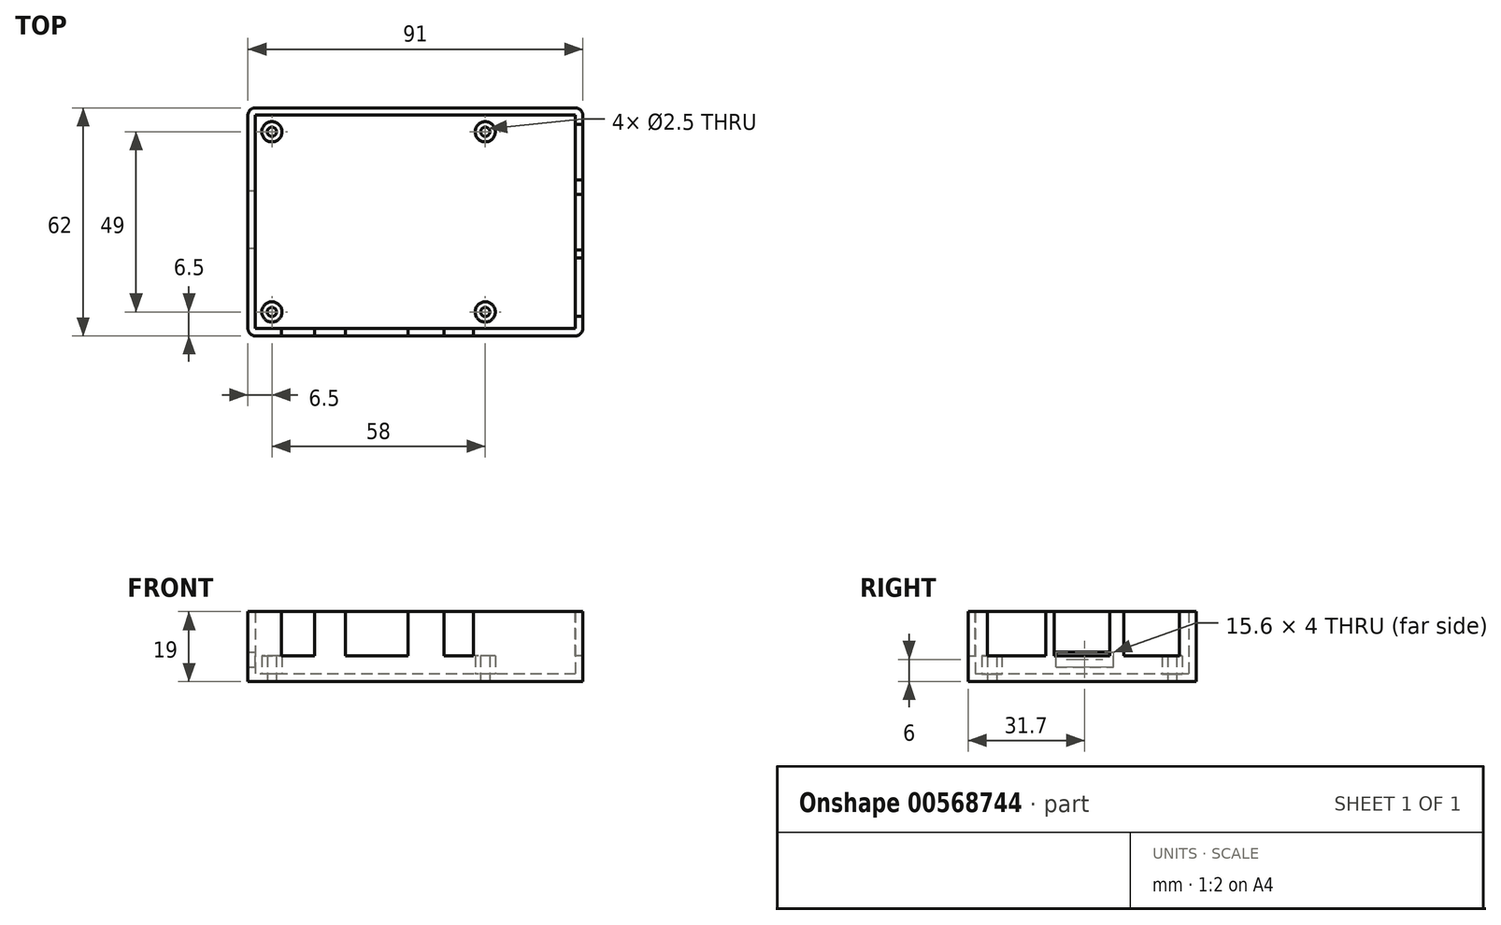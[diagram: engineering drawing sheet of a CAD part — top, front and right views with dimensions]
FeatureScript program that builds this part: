
annotation { "Feature Type Name" : "Feature", "Feature Type Description" : "" }
export const myFeature = defineFeature(function(context is Context, id is Id, definition is map)
    precondition{}
    {
        {
            var Q0;
            Q0=qCreatedBy(makeId("Top.planeOp"),FACE);
            var sketch = newSketch(context, id + "F0", { "sketchPlane" : qUnion([Q0])});
            skLineSegment(sketch, "E0.bottom", {"start": v(0, 0) * mm, "end": v(91, 0) * mm});
            skLineSegment(sketch, "E0.top", {"start": v(0, 62) * mm, "end": v(91, 62) * mm});
            skLineSegment(sketch, "E0.left", {"start": v(0, 0) * mm, "end": v(0, 62) * mm});
            skLineSegment(sketch, "E0.right", {"start": v(91, 0) * mm, "end": v(91, 62) * mm});
            skLineSegment(sketch, "E1.0", {"start": v(2, 60) * mm, "end": v(89, 60) * mm});
            skLineSegment(sketch, "E1.1", {"start": v(2, 2) * mm, "end": v(2, 60) * mm});
            skLineSegment(sketch, "E1.2", {"start": v(2, 2) * mm, "end": v(89, 2) * mm});
            skLineSegment(sketch, "E1.3", {"start": v(89, 2) * mm, "end": v(89, 60) * mm});
            skLineSegment(sketch, "E2.0", {"start": v(3, 59) * mm, "end": v(88, 59) * mm, "construction": true});
            skLineSegment(sketch, "E2.1", {"start": v(3, 3) * mm, "end": v(3, 59) * mm, "construction": true});
            skLineSegment(sketch, "E2.2", {"start": v(3, 3) * mm, "end": v(88, 3) * mm, "construction": true});
            skLineSegment(sketch, "E2.3", {"start": v(88, 3) * mm, "end": v(88, 59) * mm, "construction": true});
            skSolve(sketch);
        }
        {
            var Q0;
            Q0=makeQuery(id+"F0.imprint","IMPRINT",FACE,{"disambiguationData":[TD([[makeQuery(id+"F0.imprint","IMPRINT",EDGE,{"derivedFrom":sQuery(id+"F0.wireOp",EDGE,"E0.bottom")}),1.0]])]});
            var Q1;
            Q1=makeQuery(id+"F0.imprint","IMPRINT",FACE,{"disambiguationData":[TD([[makeQuery(id+"F0.imprint","IMPRINT",EDGE,{"derivedFrom":sQuery(id+"F0.wireOp",EDGE,"E1.0")}),-1.0]])]});
            var Q2;
            Q2=makeQuery(id+"F0.imprint","IMPRINT",FACE,{"disambiguationData":[TD([[makeQuery(id+"F0.imprint","IMPRINT",EDGE,{"derivedFrom":sQuery(id+"F0.wireOp",EDGE,"70Z1q3uj-Ijsq-j34Q-QLTl-TNYluKwycWAc")}),-1.0]])]});
            var Q3;
            Q3=makeQuery(id+"F0.imprint","IMPRINT",FACE,{"disambiguationData":[TD([[makeQuery(id+"F0.imprint","IMPRINT",EDGE,{"derivedFrom":sQuery(id+"F0.wireOp",EDGE,"70Z1q3uj-Ijsq-j34Q-QLTl-TNYluKwycWAc")}),1.0]])]});
            var Q4;
            Q4=makeQuery(id+"F0.imprint","IMPRINT",FACE,{"disambiguationData":[TD([[makeQuery(id+"F0.imprint","IMPRINT",EDGE,{"derivedFrom":sQuery(id+"F0.wireOp",EDGE,"oQS00QZW-vNgy-keFn-j1EO-3NQ6BuG1DB5t")}),1.0]])]});
            var Q5;
            Q5=makeQuery(id+"F0.imprint","IMPRINT",FACE,{"disambiguationData":[TD([[makeQuery(id+"F0.imprint","IMPRINT",EDGE,{"derivedFrom":sQuery(id+"F0.wireOp",EDGE,"oQS00QZW-vNgy-keFn-j1EO-3NQ6BuG1DB5t")}),-1.0]])]});
            var Q6;
            Q6=makeQuery(id+"F0.imprint","IMPRINT",FACE,{"disambiguationData":[TD([[makeQuery(id+"F0.imprint","IMPRINT",EDGE,{"derivedFrom":sQuery(id+"F0.wireOp",EDGE,"wAKH25U2-zgrz-eWns-j4sG-55EGYDsWBGuE")}),-1.0]])]});
            var Q7;
            Q7=makeQuery(id+"F0.imprint","IMPRINT",FACE,{"disambiguationData":[TD([[makeQuery(id+"F0.imprint","IMPRINT",EDGE,{"derivedFrom":sQuery(id+"F0.wireOp",EDGE,"wAKH25U2-zgrz-eWns-j4sG-55EGYDsWBGuE")}),1.0]])]});
            var Q8;
            Q8=makeQuery(id+"F0.imprint","IMPRINT",FACE,{"disambiguationData":[TD([[makeQuery(id+"F0.imprint","IMPRINT",EDGE,{"derivedFrom":sQuery(id+"F0.wireOp",EDGE,"CY4kjaGw-B2gw-ZOHd-aq1m-nUtJw6pQ65pw")}),-1.0]])]});
            var Q9;
            Q9=makeQuery(id+"F0.imprint","IMPRINT",FACE,{"disambiguationData":[TD([[makeQuery(id+"F0.imprint","IMPRINT",EDGE,{"derivedFrom":sQuery(id+"F0.wireOp",EDGE,"CY4kjaGw-B2gw-ZOHd-aq1m-nUtJw6pQ65pw")}),1.0]])]});
            extrude(context, id + "F1", {"entities" : qUnion([Q0, Q1, Q2, Q3, Q4, Q5, Q6, Q7, Q8, Q9]), "depth" : 2 * mm, "offsetDistance" : 25 * mm});
        }
        {
            var Q0;
            Q0 = qSketchRegion(id + "F0", true);
            extrude(context, id + "F2", {"entities" : qUnion([Q0]), "operationType" : NewBodyOperationType.ADD, "depth" : 19 * mm, "offsetDistance" : 25 * mm});
        }
        {
            var Q0;
            Q0=makeQuery(id+"F1.opExtrude","CAP_FACE",FACE,{"disambiguationData":[OSD([sQuery(id+"F0.wireOp",EDGE,"E0.bottom"),sQuery(id+"F0.wireOp",EDGE,"E0.top"),sQuery(id+"F0.wireOp",EDGE,"E0.left"),sQuery(id+"F0.wireOp",EDGE,"E0.right")])],"isStart":false});
            var sketch = newSketch(context, id + "F3", { "sketchPlane" : qUnion([Q0])});
            skCircle(sketch, "E3", {"center": v(6.5, 55.5) * mm, "radius": 1.25 * mm});
            skCircle(sketch, "E4", {"center": v(6.5, 55.5) * mm, "radius": 2.75 * mm});
            skCircle(sketch, "E5", {"center": v(64.5, 55.5) * mm, "radius": 1.25 * mm});
            skCircle(sketch, "E6", {"center": v(64.5, 55.5) * mm, "radius": 2.75 * mm});
            skCircle(sketch, "E7", {"center": v(64.5, 6.5) * mm, "radius": 1.25 * mm});
            skCircle(sketch, "E8", {"center": v(64.5, 6.5) * mm, "radius": 2.75 * mm});
            skCircle(sketch, "E9", {"center": v(6.5, 6.5) * mm, "radius": 1.25 * mm});
            skCircle(sketch, "E10", {"center": v(6.5, 6.5) * mm, "radius": 2.75 * mm});
            skSolve(sketch);
        }
        {
            var Q0;
            Q0 = qSketchRegion(id + "F3", true);
            extrude(context, id + "F4", {"entities" : qUnion([Q0]), "operationType" : NewBodyOperationType.ADD, "depth" : 5 * mm, "offsetDistance" : 25 * mm});
        }
        {
            var Q0;
            Q0=makeQuery(id+"F4.boolean.opBoolean","SPLIT",FACE,{"disambiguationData":[TD([makeQuery(id+"F4.opExtrude","SWEPT_FACE",FACE,{"disambiguationData":[OSD([sQuery(id+"F3.wireOp",EDGE,"E3")])]})])],"derivedFrom":makeQuery(id+"F1.opExtrude","CAP_FACE",FACE,{"disambiguationData":[OSD([sQuery(id+"F0.wireOp",EDGE,"E0.bottom"),sQuery(id+"F0.wireOp",EDGE,"E0.top"),sQuery(id+"F0.wireOp",EDGE,"E0.left"),sQuery(id+"F0.wireOp",EDGE,"E0.right")])],"isStart":false})});
            var Q1;
            Q1=makeQuery(id+"F4.boolean.opBoolean","SPLIT",FACE,{"disambiguationData":[TD([makeQuery(id+"F4.opExtrude","SWEPT_FACE",FACE,{"disambiguationData":[OSD([sQuery(id+"F3.wireOp",EDGE,"E5")])]})])],"derivedFrom":makeQuery(id+"F1.opExtrude","CAP_FACE",FACE,{"disambiguationData":[OSD([sQuery(id+"F0.wireOp",EDGE,"E0.bottom"),sQuery(id+"F0.wireOp",EDGE,"E0.top"),sQuery(id+"F0.wireOp",EDGE,"E0.left"),sQuery(id+"F0.wireOp",EDGE,"E0.right")])],"isStart":false})});
            var Q2;
            Q2=makeQuery(id+"F4.boolean.opBoolean","SPLIT",FACE,{"disambiguationData":[TD([makeQuery(id+"F4.opExtrude","SWEPT_FACE",FACE,{"disambiguationData":[OSD([sQuery(id+"F3.wireOp",EDGE,"E7")])]})])],"derivedFrom":makeQuery(id+"F1.opExtrude","CAP_FACE",FACE,{"disambiguationData":[OSD([sQuery(id+"F0.wireOp",EDGE,"E0.bottom"),sQuery(id+"F0.wireOp",EDGE,"E0.top"),sQuery(id+"F0.wireOp",EDGE,"E0.left"),sQuery(id+"F0.wireOp",EDGE,"E0.right")])],"isStart":false})});
            var Q3;
            Q3=makeQuery(id+"F4.boolean.opBoolean","SPLIT",FACE,{"disambiguationData":[TD([makeQuery(id+"F4.opExtrude","SWEPT_FACE",FACE,{"disambiguationData":[OSD([sQuery(id+"F3.wireOp",EDGE,"E9")])]})])],"derivedFrom":makeQuery(id+"F1.opExtrude","CAP_FACE",FACE,{"disambiguationData":[OSD([sQuery(id+"F0.wireOp",EDGE,"E0.bottom"),sQuery(id+"F0.wireOp",EDGE,"E0.top"),sQuery(id+"F0.wireOp",EDGE,"E0.left"),sQuery(id+"F0.wireOp",EDGE,"E0.right")])],"isStart":false})});
            extrude(context, id + "F5", {"entities" : qUnion([Q0, Q1, Q2, Q3]), "operationType" : NewBodyOperationType.REMOVE, "endBound" : BoundingType.THROUGH_ALL, "oppositeDirection" : true, "depth" : 25 * mm, "offsetDistance" : 25 * mm});
        }
        {
            var Q0;
            Q0=makeQuery(id+"F2.opExtrude","CAP_FACE",FACE,{"disambiguationData":[OSD([sQuery(id+"F0.wireOp",EDGE,"E0.bottom"),sQuery(id+"F0.wireOp",EDGE,"E0.top"),sQuery(id+"F0.wireOp",EDGE,"E0.left"),sQuery(id+"F0.wireOp",EDGE,"E0.right"),sQuery(id+"F0.wireOp",EDGE,"E1.0"),sQuery(id+"F0.wireOp",EDGE,"E1.1"),sQuery(id+"F0.wireOp",EDGE,"E1.2"),sQuery(id+"F0.wireOp",EDGE,"E1.3")])],"isStart":false});
            var sketch = newSketch(context, id + "F6", { "sketchPlane" : qUnion([Q0])});
            skLineSegment(sketch, "E11.bottom", {"start": v(88, 57.5) * mm, "end": v(91, 57.5) * mm});
            skLineSegment(sketch, "E11.top", {"start": v(88, 42.4) * mm, "end": v(91, 42.4) * mm});
            skLineSegment(sketch, "E11.left", {"start": v(88, 57.5) * mm, "end": v(88, 42.4) * mm});
            skLineSegment(sketch, "E11.right", {"start": v(91, 57.5) * mm, "end": v(91, 42.4) * mm});
            skLineSegment(sketch, "E12.bottom", {"start": v(88, 38.5) * mm, "end": v(91, 38.5) * mm});
            skLineSegment(sketch, "E12.top", {"start": v(88, 23.4) * mm, "end": v(91, 23.4) * mm});
            skLineSegment(sketch, "E12.left", {"start": v(88, 38.5) * mm, "end": v(88, 23.4) * mm});
            skLineSegment(sketch, "E12.right", {"start": v(91, 38.5) * mm, "end": v(91, 23.4) * mm});
            skLineSegment(sketch, "E13.bottom", {"start": v(88, 21.2) * mm, "end": v(91, 21.2) * mm});
            skLineSegment(sketch, "E13.top", {"start": v(88, 5.3) * mm, "end": v(91, 5.3) * mm});
            skLineSegment(sketch, "E13.left", {"start": v(88, 21.2) * mm, "end": v(88, 5.3) * mm});
            skLineSegment(sketch, "E13.right", {"start": v(91, 21.2) * mm, "end": v(91, 5.3) * mm});
            skLineSegment(sketch, "E14.bottom", {"start": v(9.05, 2) * mm, "end": v(18.05, 2) * mm});
            skLineSegment(sketch, "E14.top", {"start": v(9.05, 0) * mm, "end": v(18.05, 0) * mm});
            skLineSegment(sketch, "E14.left", {"start": v(9.05, 2) * mm, "end": v(9.05, 0) * mm});
            skLineSegment(sketch, "E14.right", {"start": v(18.05, 2) * mm, "end": v(18.05, 0) * mm});
            skLineSegment(sketch, "E15.bottom", {"start": v(26.5, 2) * mm, "end": v(43.5, 2) * mm});
            skLineSegment(sketch, "E15.top", {"start": v(26.5, 0) * mm, "end": v(43.5, 0) * mm});
            skLineSegment(sketch, "E15.left", {"start": v(26.5, 2) * mm, "end": v(26.5, 0) * mm});
            skLineSegment(sketch, "E15.right", {"start": v(43.5, 2) * mm, "end": v(43.5, 0) * mm});
            skLineSegment(sketch, "E16.bottom", {"start": v(53.25, 2) * mm, "end": v(61.25, 2) * mm});
            skLineSegment(sketch, "E16.top", {"start": v(53.25, 0) * mm, "end": v(61.25, 0) * mm});
            skLineSegment(sketch, "E16.left", {"start": v(53.25, 2) * mm, "end": v(53.25, 0) * mm});
            skLineSegment(sketch, "E16.right", {"start": v(61.25, 2) * mm, "end": v(61.25, 0) * mm});
            skPoint(sketch, "E17", {"position": v(13.55, 2) * mm});
            skPoint(sketch, "E18", {"position": v(35, 2) * mm});
            skPoint(sketch, "E19", {"position": v(57.25, 2) * mm});
            skSolve(sketch);
        }
        {
            var Q0;
            Q0 = qSketchRegion(id + "F6", true);
            var Q1;
            Q1=makeQuery(id+"F4.opExtrude","CAP_FACE",FACE,{"disambiguationData":[OSD([sQuery(id+"F3.wireOp",EDGE,"E9"),sQuery(id+"F3.wireOp",EDGE,"E10")])],"isStart":false});
            extrude(context, id + "F7", {"entities" : qUnion([Q0]), "operationType" : NewBodyOperationType.REMOVE, "endBound" : BoundingType.UP_TO_SURFACE, "oppositeDirection" : true, "depth" : 25 * mm, "endBoundEntityFace" : qUnion([Q1]), "offsetDistance" : 25 * mm});
        }
        {
            var Q0;
            {var subQ0=sQuery(id+"F0.wireOp",EDGE,"E0.right");var subQ1=sQuery(id+"F0.wireOp",EDGE,"E0.bottom");Q0=makeQuery(id+"F2.boolean.opBoolean","MERGE",EDGE,{"derivedFrom":[makeQuery(id+"F1.opExtrude","SWEPT_EDGE",EDGE,{"disambiguationData":[OSD([subQ1,subQ0])]}),makeQuery(id+"F2.opExtrude","SWEPT_EDGE",EDGE,{"disambiguationData":[OSD([subQ1,subQ0])]})]});}
            var Q1;
            {var subQ0=sQuery(id+"F0.wireOp",EDGE,"E0.right");var subQ1=sQuery(id+"F0.wireOp",EDGE,"E0.top");Q1=makeQuery(id+"F2.boolean.opBoolean","MERGE",EDGE,{"derivedFrom":[makeQuery(id+"F1.opExtrude","SWEPT_EDGE",EDGE,{"disambiguationData":[OSD([subQ1,subQ0])]}),makeQuery(id+"F2.opExtrude","SWEPT_EDGE",EDGE,{"disambiguationData":[OSD([subQ1,subQ0])]})]});}
            var Q2;
            {var subQ0=sQuery(id+"F0.wireOp",EDGE,"E0.left");var subQ1=sQuery(id+"F0.wireOp",EDGE,"E0.bottom");Q2=makeQuery(id+"F2.boolean.opBoolean","MERGE",EDGE,{"derivedFrom":[makeQuery(id+"F1.opExtrude","SWEPT_EDGE",EDGE,{"disambiguationData":[OSD([subQ1,subQ0])]}),makeQuery(id+"F2.opExtrude","SWEPT_EDGE",EDGE,{"disambiguationData":[OSD([subQ1,subQ0])]})]});}
            var Q3;
            {var subQ0=sQuery(id+"F0.wireOp",EDGE,"E0.left");var subQ1=sQuery(id+"F0.wireOp",EDGE,"E0.top");Q3=makeQuery(id+"F2.boolean.opBoolean","MERGE",EDGE,{"derivedFrom":[makeQuery(id+"F1.opExtrude","SWEPT_EDGE",EDGE,{"disambiguationData":[OSD([subQ1,subQ0])]}),makeQuery(id+"F2.opExtrude","SWEPT_EDGE",EDGE,{"disambiguationData":[OSD([subQ1,subQ0])]})]});}
            fillet(context, id + "F8", {"entities" : qUnion([Q0, Q1, Q2, Q3]), "radius" : 2 * mm, "tangentPropagation" : true, "allowEdgeOverflow" : false});
        }
        {
            var Q0;
            Q0=makeQuery(id+"F4.opExtrude","CAP_FACE",FACE,{"disambiguationData":[OSD([sQuery(id+"F3.wireOp",EDGE,"E3"),sQuery(id+"F3.wireOp",EDGE,"E4")])],"isStart":false});
            var sketch = newSketch(context, id + "F9", { "sketchPlane" : qUnion([Q0])});
            skLineSegment(sketch, "E20.bottom", {"start": v(0, 23.9) * mm, "end": v(2, 23.9) * mm});
            skLineSegment(sketch, "E20.top", {"start": v(0, 39.5) * mm, "end": v(2, 39.5) * mm});
            skLineSegment(sketch, "E20.left", {"start": v(0, 23.9) * mm, "end": v(0, 39.5) * mm});
            skLineSegment(sketch, "E20.right", {"start": v(2, 23.9) * mm, "end": v(2, 39.5) * mm});
            skSolve(sketch);
        }
        {
            var Q0;
            Q0 = qSketchRegion(id + "F9", true);
            extrude(context, id + "F10", {"entities" : qUnion([Q0]), "operationType" : NewBodyOperationType.REMOVE, "oppositeDirection" : true, "depth" : 3 * mm, "offsetDistance" : 25 * mm, "hasSecondDirection" : true, "secondDirectionOppositeDirection" : false, "secondDirectionDepth" : 1 * mm});
        }
    });
